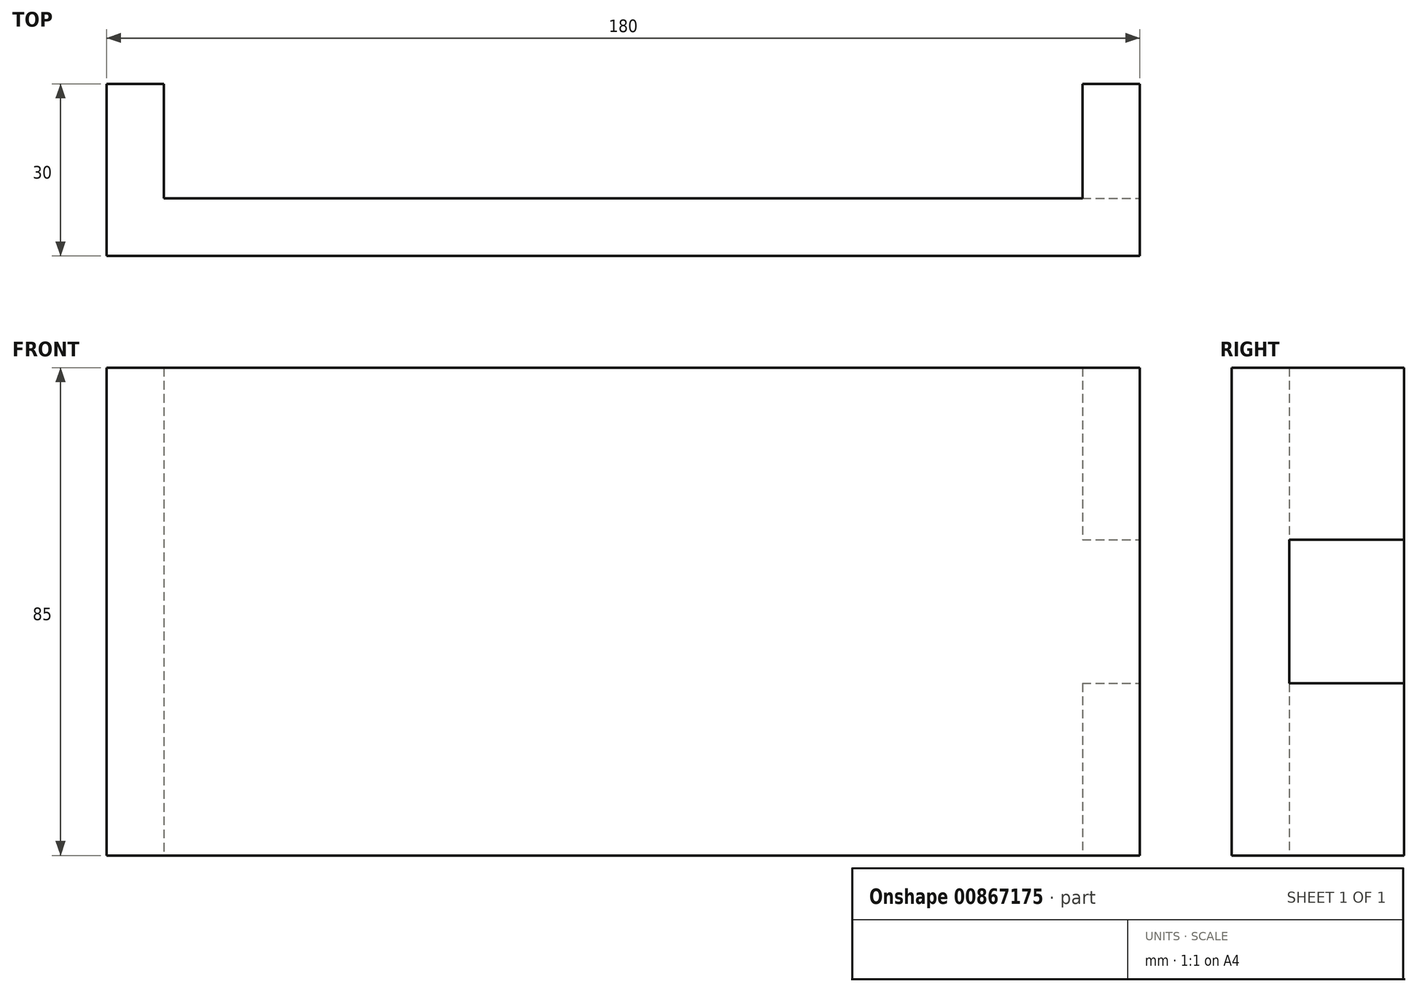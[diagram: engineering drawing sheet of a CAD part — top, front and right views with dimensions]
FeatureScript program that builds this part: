
annotation { "Feature Type Name" : "Feature", "Feature Type Description" : "" }
export const myFeature = defineFeature(function(context is Context, id is Id, definition is map)
    precondition{}
    {
        {
            var Q0;
            Q0=qCreatedBy(makeId("Top.planeOp"),FACE);
            var sketch = newSketch(context, id + "F0", { "sketchPlane" : qUnion([Q0])});
            skLineSegment(sketch, "E0", {"start": v(-180, 0) * mm, "end": v(0, 0) * mm});
            skLineSegment(sketch, "E1", {"start": v(0, 0) * mm, "end": v(0, 30) * mm});
            skLineSegment(sketch, "E2", {"start": v(0, 30) * mm, "end": v(-10, 30) * mm});
            skLineSegment(sketch, "E3", {"start": v(-10, 30) * mm, "end": v(-10, 10) * mm});
            skLineSegment(sketch, "E4", {"start": v(-10, 10) * mm, "end": v(-170, 10) * mm});
            skLineSegment(sketch, "E5", {"start": v(-170, 10) * mm, "end": v(-170, 30) * mm});
            skLineSegment(sketch, "E6", {"start": v(-170, 30) * mm, "end": v(-180, 30) * mm});
            skLineSegment(sketch, "E7", {"start": v(-180, 30) * mm, "end": v(-180, 0) * mm});
            skSolve(sketch);
        }
        {
            var Q0;
            Q0=makeQuery(id+"F0.imprint","IMPRINT",FACE,{"disambiguationData":[TD([[makeQuery(id+"F0.imprint","IMPRINT",EDGE,{"derivedFrom":sQuery(id+"F0.wireOp",EDGE,"E0")}),1.0]])]});
            extrude(context, id + "F1", {"entities" : qUnion([Q0]), "depth" : 10 * mm, "offsetDistance" : 25 * mm});
        }
        {
            var Q0;
            Q0=makeQuery(id+"F1.opExtrude","CAP_FACE",FACE,{"disambiguationData":[OSD([sQuery(id+"F0.wireOp",EDGE,"E0"),sQuery(id+"F0.wireOp",EDGE,"E1"),sQuery(id+"F0.wireOp",EDGE,"E2"),sQuery(id+"F0.wireOp",EDGE,"E3"),sQuery(id+"F0.wireOp",EDGE,"E4"),sQuery(id+"F0.wireOp",EDGE,"E5"),sQuery(id+"F0.wireOp",EDGE,"E6"),sQuery(id+"F0.wireOp",EDGE,"E7")])],"isStart":false});
            extrude(context, id + "F2", {"entities" : qUnion([Q0]), "operationType" : NewBodyOperationType.ADD, "oppositeDirection" : true, "depth" : 85 * mm, "offsetDistance" : 25 * mm});
        }
        {
            var Q0;
            {var subQ0=sQuery(id+"F0.wireOp",EDGE,"E1");Q0=makeQuery(id+"F2.boolean.opBoolean","MERGE",FACE,{"derivedFrom":[makeQuery(id+"F1.opExtrude","SWEPT_FACE",FACE,{"disambiguationData":[OSD([subQ0])]}),makeQuery(id+"F2.opExtrude","SWEPT_FACE",FACE,{"disambiguationData":[OSD([subQ0])]})]});}
            var sketch = newSketch(context, id + "F3", { "sketchPlane" : qUnion([Q0])});
            skLineSegment(sketch, "E8", {"start": v(30, -20) * mm, "end": v(10, -20) * mm});
            skLineSegment(sketch, "E9", {"start": v(10, -20) * mm, "end": v(10, -45) * mm});
            skLineSegment(sketch, "E10", {"start": v(10, -45) * mm, "end": v(30, -45) * mm});
            skSolve(sketch);
        }
        {
            var Q0;
            {var subQ0=sQuery(id+"F3.wireOp",EDGE,"E8");Q0=makeQuery(id+"F3.imprint","IMPRINT",FACE,{"disambiguationData":[TD([[makeQuery(id+"F3.imprint","IMPRINT",EDGE,{"derivedFrom":subQ0}),1.0]])]});}
            extrude(context, id + "F4", {"entities" : qUnion([Q0]), "operationType" : NewBodyOperationType.REMOVE, "oppositeDirection" : true, "depth" : 88.4 * mm, "offsetDistance" : 25 * mm});
        }
    });
